# Revit family: Sanitary_Showers_hansgrohe_26279XXX-Vernis-Blend-Shower-set-Vario-E_01
name_source: partatom
category: Plumbing Fixtures
units: mm (PartAtom-declared; Revit-internal decimal feet)

## family parameters
Always vertical = No
Cut with Voids When Loaded = No
OmniClass Number = 23.31.17.00
OmniClass Title = Showers
Part Type = Normal
Room Calculation Point = No
Round Connector Dimension = Use Diameter
Shared = No
Work Plane-Based = Yes

## types (1)
- 000 Chrome
    Default Elevation = 1219 mm
    Description = Vernis Blend Shower set 100 Vario EcoSmart with shower bar Crometta 65 cm
    Manufacturer = Hansgrohe
    Material = Hansgrohe - Metal - 000 Chrome
    Material 1 = Hansgrohe - Plastic - Gray
    Model = 26279XXX
    Product Guid = b6f8ffa3-cb2d-4bea-b7f7-e453531de06c
    Product Page URL = https://pro.hansgrohe.com
    Product data url = https://bimobject.com
    URL = https://www.hansgrohe.com
    Version = 1

## geometry (parser evidence)
native form markers: Blend x6, Sweep x2
no freeform markers — native parametric forms only
